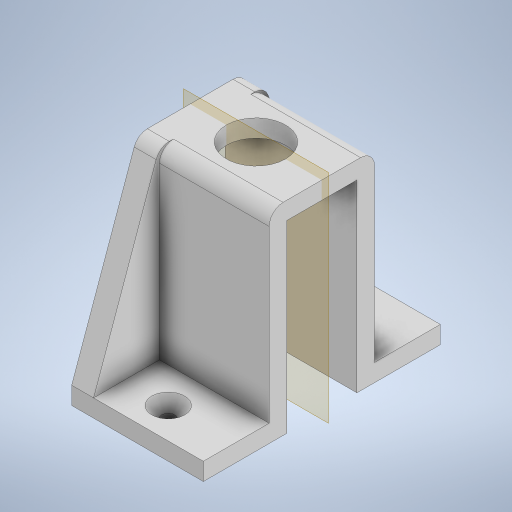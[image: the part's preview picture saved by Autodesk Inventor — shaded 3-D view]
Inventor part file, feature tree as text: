
AUTODESK INVENTOR PART (.ipt)
format: ipt  version: 2024 (Build 280153020, 153B)  size: 302,592 bytes
history: native  units: in
note: dims shown in document units (in); Inventor stores cm internally (conversion verified against a paired STEP export)
features: sketch x6, extrude x5, plane x1, hole x1, mirror x1, fillet x1
ambient origin geometry x8: Origin, YZ Plane, XZ Plane, XY Plane, X Axis, Y Axis, Z Axis, Center Point
bodies: Body1 (feature_tree)
feature tree (15):
  extrude  "Extrusion2"  Depth=0.9449in
  extrude  "Extrusion3"  Depth=0.1575in
  extrude  "Extrusion4"  Depth=1.6535in TaperAngle=0.0deg
  plane  "Work Plane1"
  extrude  "Extrusion5"  Depth=0.5906in TaperAngle=0.0deg
  hole  "Hole1"  [1 undecoded]
  extrude  "Extrusion6"  Depth=0.1969in TaperAngle=0.0deg
  mirror  "Mirror1"
  fillet  "Fillet2"  Radius=0.125in
  sketch  "Sketch2"  dims[d5=1.1811in d6=0.9449in]
  sketch  "Sketch3"  dims[d7=0.1575in d8=0.0in d9=0.1575in]
  sketch  "Sketch4"  dims[d10=0.1575in d11=1.6535in d12=0.0in]
  sketch  "Sketch5"  dims[d13=0.1575in d14=0.5906in d15=0.0in]
  sketch  "Sketch6"  dims[d16=0.53in d17=0.5969in d18=0.0in]
  sketch  "Sketch7"  dims[d19=0.2756in d20=0.1181in d21=0.75in d22=0.2953in d23=0.25in d24=0.5635in d25=1.0in d26=0.8108in d27=0.1969in d28=0.0in d29=0.125in]
note: 1 required parameter value undecoded (feature->parameter linkage not recoverable at this tier; creation-order binding heuristic only, values carry confidence <= 0.55)
